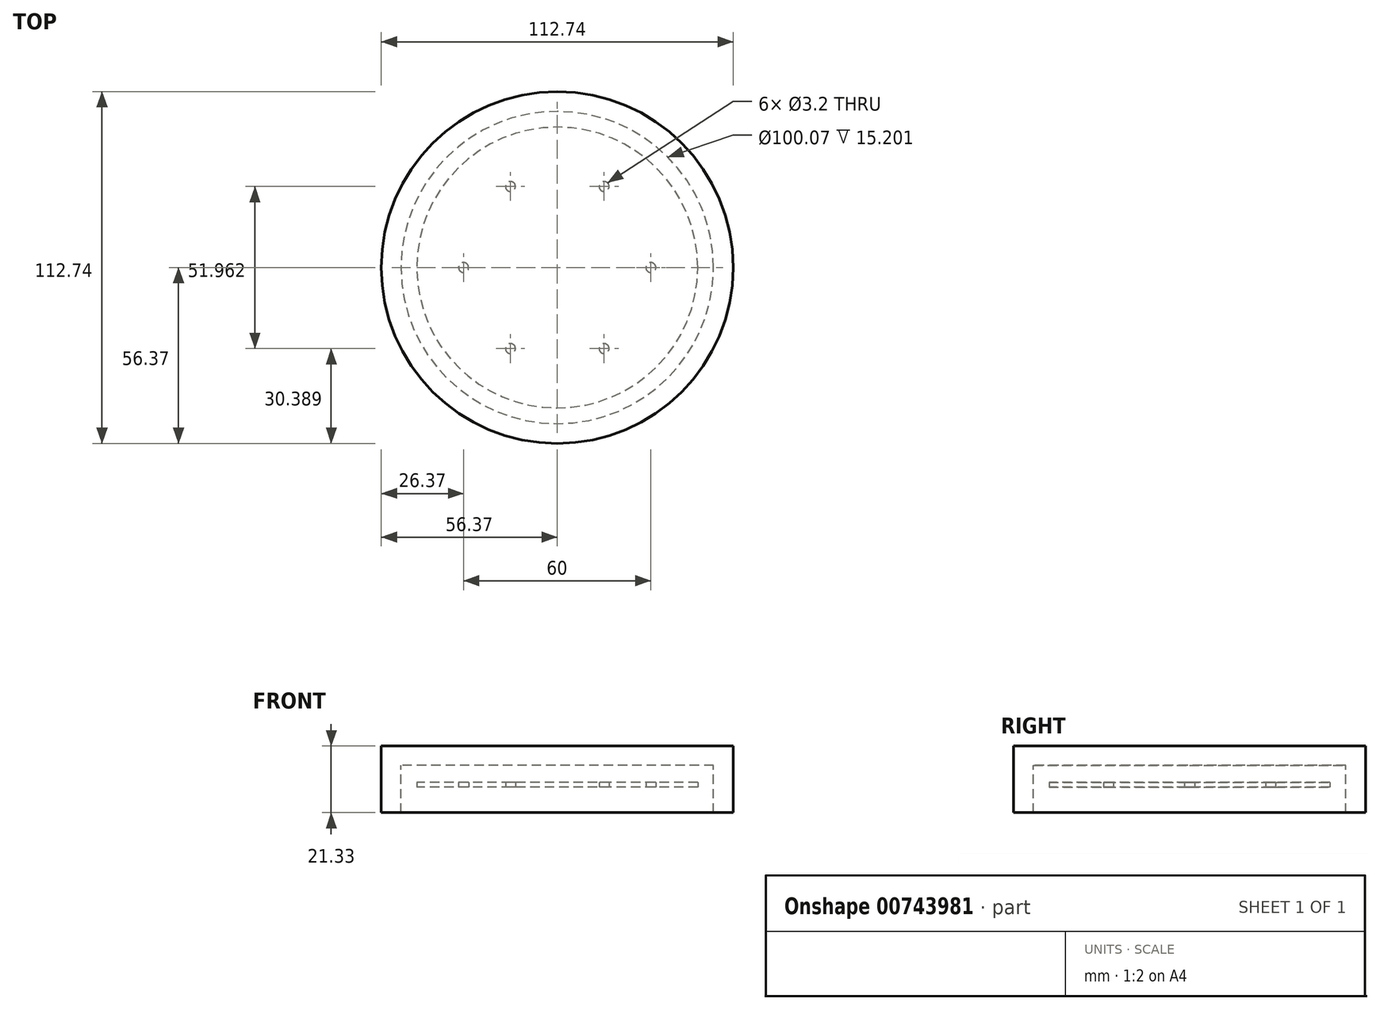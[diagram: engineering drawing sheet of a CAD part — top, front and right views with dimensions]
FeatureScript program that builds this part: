
annotation { "Feature Type Name" : "Feature", "Feature Type Description" : "" }
export const myFeature = defineFeature(function(context is Context, id is Id, definition is map)
    precondition{}
    {
        {
            var Q0;
            Q0=qCreatedBy(makeId("Top.planeOp"),FACE);
            var sketch = newSketch(context, id + "F0", { "sketchPlane" : qUnion([Q0])});
            skCircle(sketch, "E0", {"center": v(0, 0) * mm, "radius": 45 * mm});
            skCircle(sketch, "E1", {"center": v(15, 25.98) * mm, "radius": 1.6 * mm});
            skCircle(sketch, "E2.1.0", {"center": v(-15, 25.98) * mm, "radius": 1.6 * mm});
            skCircle(sketch, "E2.2.0", {"center": v(-30, 0) * mm, "radius": 1.6 * mm});
            skCircle(sketch, "E2.3.0", {"center": v(-15, -25.98) * mm, "radius": 1.6 * mm});
            skCircle(sketch, "E2.4.0", {"center": v(15, -25.98) * mm, "radius": 1.6 * mm});
            skCircle(sketch, "E2.5.0", {"center": v(30, 0) * mm, "radius": 1.6 * mm});
            skSolve(sketch);
        }
        {
            var Q0;
            Q0 = qSketchRegion(id + "F0", true);
            extrude(context, id + "F1", {"entities" : qUnion([Q0]), "depth" : 1.6 * mm, "offsetDistance" : 25 * mm});
        }
        {
            var Q0;
            Q0=qCreatedBy(makeId("Right.planeOp"),FACE);
            var sketch = newSketch(context, id + "F2", { "sketchPlane" : qUnion([Q0])});
            skLineSegment(sketch, "E3", {"start": v(0, 7.07) * mm, "end": v(50.04, 7.07) * mm});
            skLineSegment(sketch, "E4", {"start": v(50.04, 7.07) * mm, "end": v(50.04, -8.13) * mm});
            skLineSegment(sketch, "E5", {"start": v(50.04, -8.13) * mm, "end": v(56.37, -8.13) * mm});
            skLineSegment(sketch, "E6", {"start": v(56.37, -8.13) * mm, "end": v(56.37, 13.2) * mm});
            skLineSegment(sketch, "E7", {"start": v(56.37, 13.2) * mm, "end": v(0, 13.2) * mm});
            skLineSegment(sketch, "E8", {"start": v(0, 13.2) * mm, "end": v(0, 7.07) * mm});
            skSolve(sketch);
        }
        {
            var Q0;
            Q0=makeQuery(id+"F2.imprint","IMPRINT",FACE,{"disambiguationData":[TD([[makeQuery(id+"F2.imprint","IMPRINT",EDGE,{"derivedFrom":sQuery(id+"F2.wireOp",EDGE,"E3")}),1.0]])]});
            var Q1;
            Q1=sQuery(id+"F2.wireOp",EDGE,"E8");
            revolve(context, id + "F3", {"surfaceOperationType" : NewSurfaceOperationType.NEW, "entities" : qUnion([Q0]), "axis" : qUnion([Q1]), "revolveType" : RevolveType.FULL});
        }
    });
